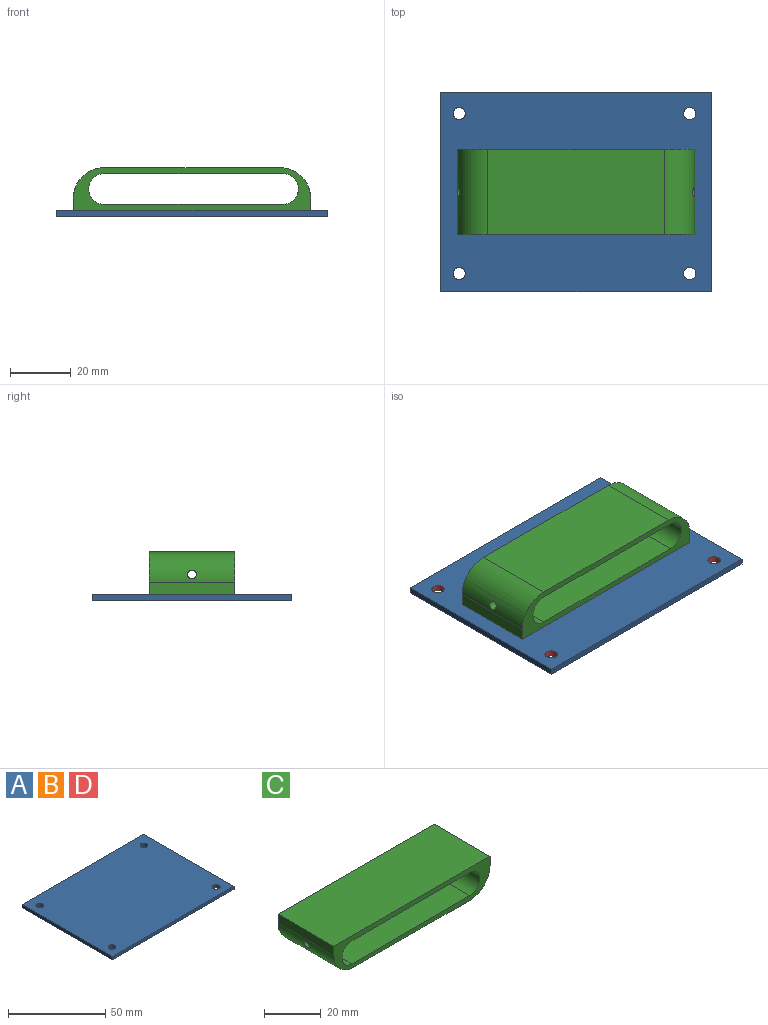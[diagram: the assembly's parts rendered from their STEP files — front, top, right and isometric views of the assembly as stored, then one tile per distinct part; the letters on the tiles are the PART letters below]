
ASSEMBLY  parts=4 mates=1
PART A: 10 faces, bbox 88.8x65.6x2 mm
  f0: plane 88.8x2mm, normal (0,1,0), area 177.6mm2, adj f1,f7,f8,f9
  f1: plane 65.6x2mm, normal (-1,0,0), area 131.2mm2, adj f0,f2,f8,f9
  f2: plane 88.8x2mm, normal (0,-1,0), area 177.6mm2, adj f1,f7,f8,f9
  f3: cylinder r=2mm len=4mm, axis (0,0,-1), area 25.1mm2, adj f8,f9
  f4: cylinder r=2mm len=4mm, axis (0,0,-1), area 25.1mm2, adj f8,f9
  f5: cylinder r=2mm len=4mm, axis (0,0,-1), area 25.1mm2, adj f8,f9
  f6: cylinder r=2mm len=4mm, axis (0,0,-1), area 25.1mm2, adj f8,f9
  f7: plane 65.6x2mm, normal (1,0,0), area 131.2mm2, adj f0,f2,f8,f9
  f8: plane 88.8x65.6mm, normal (0,0,1), area 5775mm2, adj f0,f1,f2,f3,f4,f5,f6,f7
  f9: plane 88.8x65.6mm, normal (0,0,-1), area 5775mm2, adj f0,f1,f2,f3,f4,f5,f6,f7
PART B: same geometry as A
PART C: 14 faces, bbox 78x28x20 mm
  f0: cylinder r=10mm len=28mm, axis (0,1,0), area 439.8mm2, adj f1,f5,f9,f10,f11
  f1: cylinder r=1.45mm len=4.34mm, axis (1,0,0), area 36.1mm2, adj f0,f3
  f2: cylinder r=5mm len=28mm, axis (0,-1,0), area 433.1mm2, adj f6,f7,f8,f9,f11
  f3: cylinder r=5mm len=28mm, axis (0,-1,0), area 433.1mm2, adj f1,f7,f8,f9,f11
  f4: cylinder r=10mm len=28mm, axis (0,-1,0), area 433mm2, adj f5,f6,f9,f11,f12
  f5: plane 58x28mm, normal (0,0,-1), area 1624mm2, adj f0,f4,f9,f11
  f6: cylinder r=1.45mm len=5.34mm, axis (1,0,0), area 48.7mm2, adj f2,f4
  f7: plane 59x28mm, normal (0,0,-1), area 1652mm2, adj f2,f3,f9,f11
  f8: plane 59x28mm, normal (0,0,1), area 1652mm2, adj f2,f3,f9,f11
  f9: plane 78x14mm, normal (0,-1,0), area 380.5mm2, adj f0,f2,f3,f4,f5,f7,f8,f10
  f10: plane 28x4mm, normal (-1,0,0), area 112mm2, adj f0,f9,f11,f13
  f11: plane 78x14mm, normal (0,1,0), area 380.5mm2, adj f0,f2,f3,f4,f5,f7,f8,f10
  f12: plane 28x4mm, normal (1,0,0), area 112mm2, adj f4,f9,f11,f13
  f13: plane 78x28mm, normal (0,0,1), area 2184mm2, adj f9,f10,f11,f12
PART D: same geometry as A
PLACE A t=(-5.76,-2.3,12.87)mm
PLACE B t=(-5.76,-2.3,12.87)mm
PLACE C rot(axis=(0,1,0),180deg) t=(-31.23,14.34,-0.33)mm
PLACE D t=(-5.76,-2.3,12.87)mm
MATE fastened C.f13 <-> B.f8  axis (0,0,-1) through (-10.23,3.34,14.87)mm
